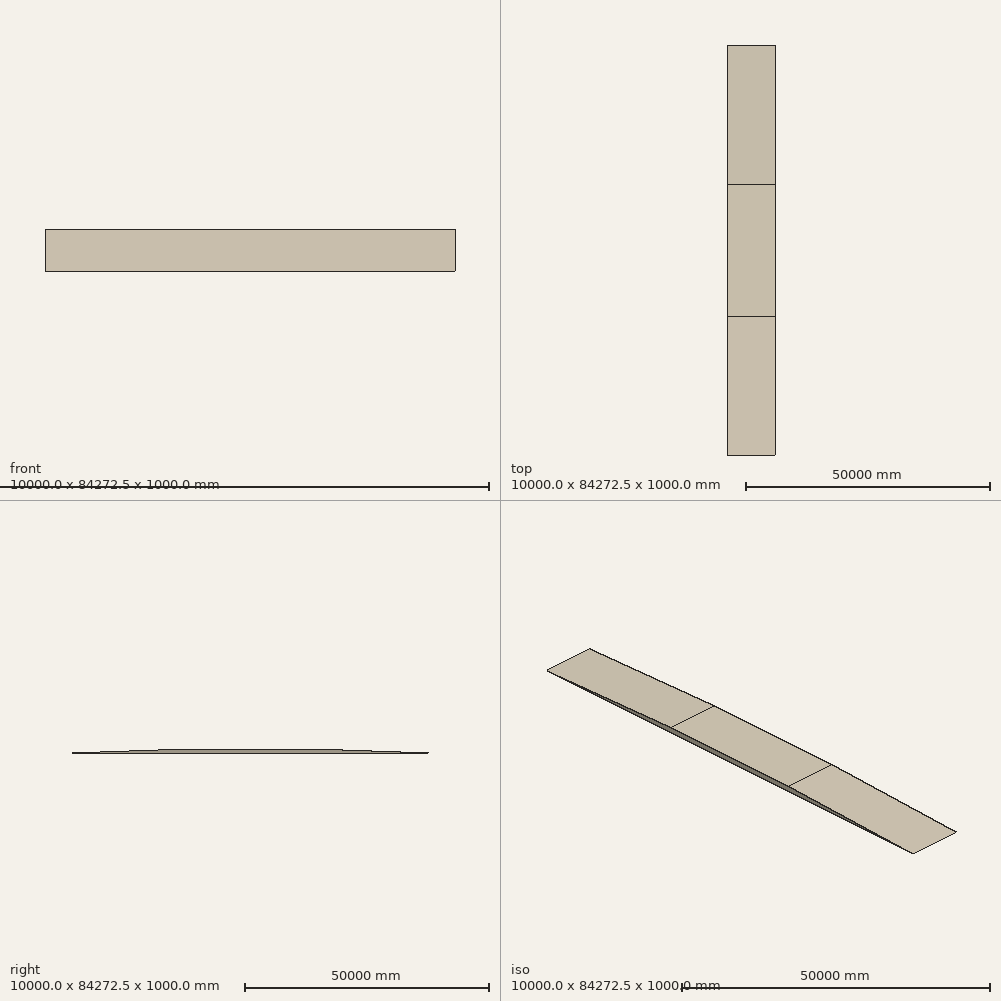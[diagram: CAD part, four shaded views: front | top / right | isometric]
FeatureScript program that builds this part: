
annotation { "Feature Type Name" : "Feature", "Feature Type Description" : "" }
export const myFeature = defineFeature(function(context is Context, id is Id, definition is map)
    precondition{}
    {
        {
            var Q0;
            Q0=qCreatedBy(makeId("Right.planeOp"),FACE);
            var sketch = newSketch(context, id + "F0", { "sketchPlane" : qUnion([Q0])});
            skLineSegment(sketch, "E0", {"start": v(9755.73, 1000) * mm, "end": v(36755.73, 1000) * mm});
            skLineSegment(sketch, "E1", {"start": v(36755.73, 1000) * mm, "end": v(65391.98, 0) * mm});
            skLineSegment(sketch, "E2", {"start": v(9755.73, 1000) * mm, "end": v(-18880.52, 0) * mm});
            skLineSegment(sketch, "E3", {"start": v(-18880.52, 0) * mm, "end": v(65391.98, 0) * mm});
            skSolve(sketch);
        }
        {
            var Q0;
            Q0 = qSketchRegion(id + "F0", true);
            extrude(context, id + "F1", {"entities" : qUnion([Q0]), "depth" : 10000 * mm});
        }
    });
